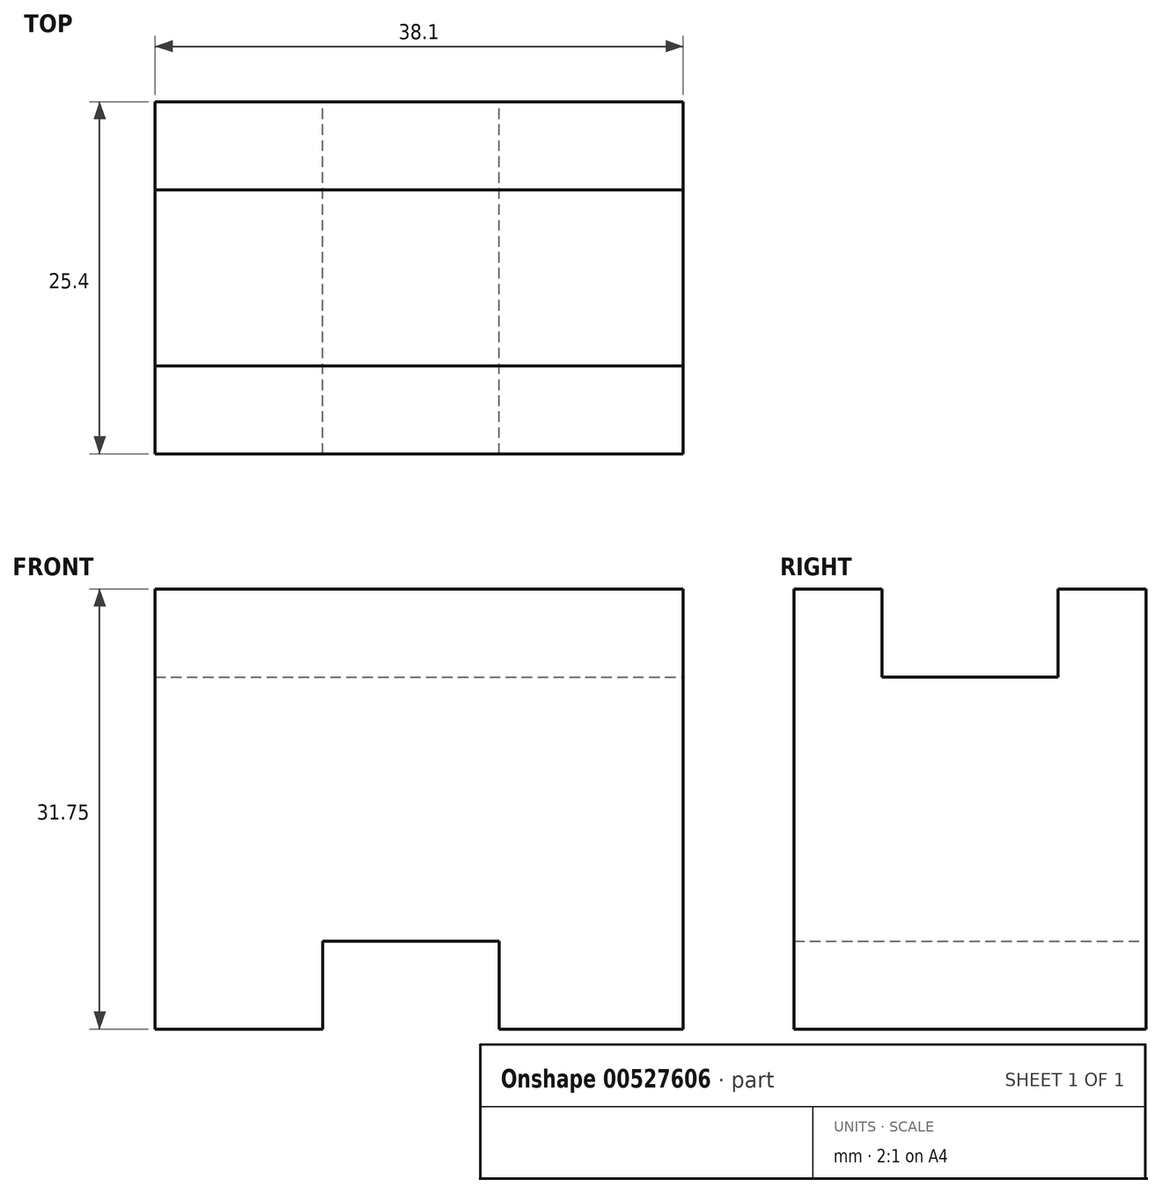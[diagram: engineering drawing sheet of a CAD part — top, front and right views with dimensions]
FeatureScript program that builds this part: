
annotation { "Feature Type Name" : "Feature", "Feature Type Description" : "" }
export const myFeature = defineFeature(function(context is Context, id is Id, definition is map)
    precondition{}
    {
        {
            var Q0;
            Q0=qCreatedBy(makeId("Right.planeOp"),FACE);
            var sketch = newSketch(context, id + "F0", { "sketchPlane" : qUnion([Q0])});
            skLineSegment(sketch, "E0", {"start": v(0, 0) * mm, "end": v(25.4, 0) * mm});
            skLineSegment(sketch, "E1", {"start": v(25.4, 0) * mm, "end": v(25.4, 31.75) * mm});
            skLineSegment(sketch, "E2", {"start": v(25.4, 31.75) * mm, "end": v(19.05, 31.75) * mm});
            skLineSegment(sketch, "E3", {"start": v(19.05, 31.75) * mm, "end": v(19.05, 25.4) * mm});
            skLineSegment(sketch, "E4", {"start": v(19.05, 25.4) * mm, "end": v(6.35, 25.4) * mm});
            skLineSegment(sketch, "E5", {"start": v(6.35, 25.4) * mm, "end": v(6.35, 31.75) * mm});
            skLineSegment(sketch, "E6", {"start": v(6.35, 31.75) * mm, "end": v(0, 31.75) * mm});
            skLineSegment(sketch, "E7", {"start": v(0, 31.75) * mm, "end": v(0, 0) * mm});
            skSolve(sketch);
        }
        {
            var Q0;
            Q0 = qSketchRegion(id + "F0", true);
            extrude(context, id + "F1", {"entities" : qUnion([Q0]), "oppositeDirection" : true, "depth" : 38.1 * mm, "offsetDistance" : 25.4 * mm});
        }
        {
            var Q0;
            Q0=makeQuery(id+"F1.opExtrude","SWEPT_FACE",FACE,{"disambiguationData":[OSD([sQuery(id+"F0.wireOp",EDGE,"E1")])]});
            var sketch = newSketch(context, id + "F2", { "sketchPlane" : qUnion([Q0])});
            skLineSegment(sketch, "E8", {"start": v(13.3, 0) * mm, "end": v(13.3, 6.35) * mm});
            skLineSegment(sketch, "E9", {"start": v(13.3, 6.35) * mm, "end": v(26, 6.35) * mm});
            skLineSegment(sketch, "E10", {"start": v(26, 6.35) * mm, "end": v(26, 0) * mm});
            skSolve(sketch);
        }
        {
            var Q0;
            Q0 = qSketchRegion(id + "F2", true);
            var Q1;
            {var subQ0=sQuery(id+"F2.wireOp",EDGE,"E8");Q1=makeQuery(id+"F2.imprint","IMPRINT",FACE,{"disambiguationData":[TD([[makeQuery(id+"F2.imprint","IMPRINT",EDGE,{"derivedFrom":subQ0}),-1.0]])]});}
            extrude(context, id + "F3", {"entities" : qUnion([Q0, Q1]), "operationType" : NewBodyOperationType.REMOVE, "oppositeDirection" : true, "depth" : 25.4 * mm, "offsetDistance" : 25.4 * mm});
        }
    });
